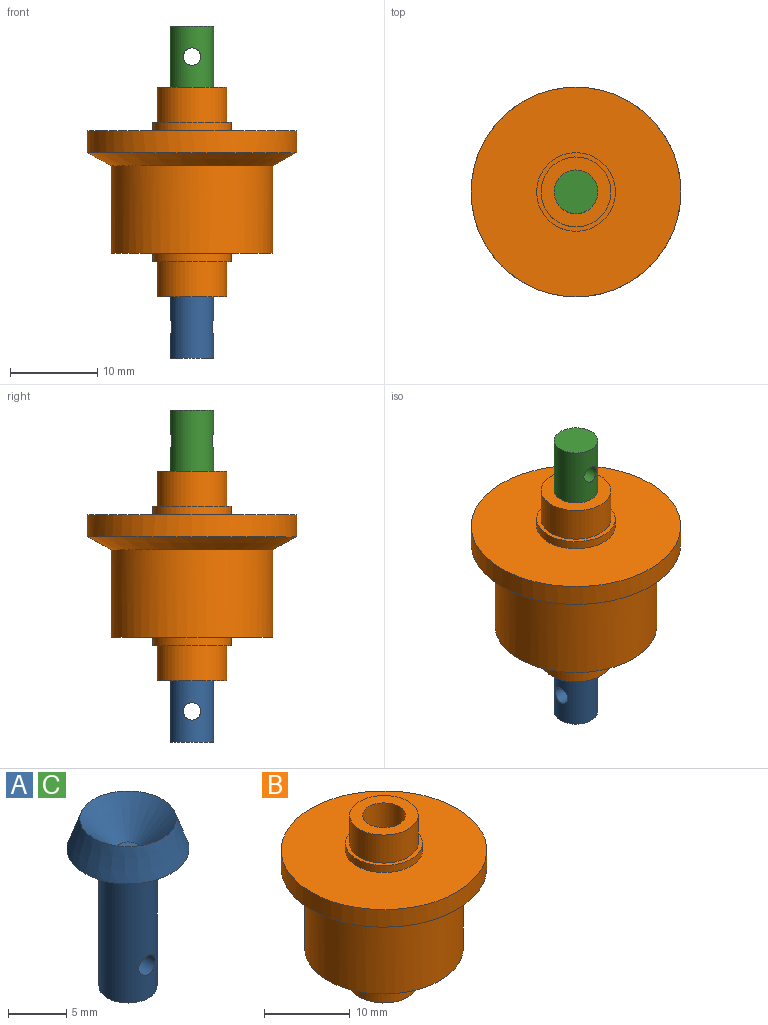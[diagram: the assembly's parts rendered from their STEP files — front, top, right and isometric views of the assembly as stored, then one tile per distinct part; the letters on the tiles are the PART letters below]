
ASSEMBLY  parts=3 mates=2
PART A: 9 faces, bbox 10.5x10.5x17.6 mm
  f0: cylinder r=2.5mm len=14mm, axis (0,0,-1), area 213.5mm2, adj f5,f6,f7
  f1: plane 10.5x10.5mm, normal (0,0,-1), area 58.3mm2, adj f2,f4
  f2: cone r=5.25mm half-angle=19.3deg, axis (0,0,-1), area 98.5mm2, adj f1,f8
  f3: plane 2x2mm, normal (0,0,1), area 3.1mm2, adj f8
  f4: cylinder r=3mm len=6mm, axis (0,0,1), area 9.4mm2, adj f1,f5
  f5: plane 6x6mm, normal (0,0,-1), area 8.6mm2, adj f0,f4
  f6: plane 5x5mm, normal (0,0,-1), area 19.6mm2, adj f0
  f7: cylinder r=1mm len=5mm, axis (0,1,0), area 30.1mm2, adj f0
  f8: cone r=1mm half-angle=45deg, axis (0,0,1), area 72mm2, adj f2,f3
PART B: 15 faces, bbox 24x24x24 mm
  f0: cylinder r=12mm len=24mm, axis (0,0,-1), area 188.5mm2, adj f1,f11
  f1: plane 24x24mm, normal (0,0,1), area 388.8mm2, adj f0,f6
  f2: cylinder r=9.25mm len=18.5mm, axis (0,0,1), area 581.2mm2, adj f3,f12
  f3: plane 18.5x18.5mm, normal (0,0,-1), area 205.2mm2, adj f2,f13
  f4: cylinder r=4mm len=8mm, axis (0,0,1), area 100.5mm2, adj f5,f14
  f5: plane 8x8mm, normal (0,0,-1), area 30.6mm2, adj f4,f10
  f6: cylinder r=4.5mm len=9mm, axis (0,0,-1), area 28.3mm2, adj f1,f7
  f7: plane 9x9mm, normal (0,0,1), area 13.4mm2, adj f6,f9
  f8: plane 8x8mm, normal (0,0,1), area 30.6mm2, adj f9,f10
  f9: cylinder r=4mm len=8mm, axis (0,0,-1), area 100.5mm2, adj f7,f8
  f10: cylinder r=2.5mm len=24mm, axis (0,0,1), area 377mm2, adj f5,f8
  f11: cone r=12mm half-angle=61.4deg, axis (0,0,1), area 209.1mm2, adj f0,f12
  f12: plane 18.5x18.5mm, normal (0,0,1), area 0mm2, adj f2,f11
  f13: cylinder r=4.5mm len=9mm, axis (0,0,1), area 28.3mm2, adj f3,f14
  f14: plane 9x9mm, normal (0,0,-1), area 13.4mm2, adj f4,f13
PART C: same geometry as A
PLACE A rot(axis=(0,0,1),90deg) t=(28.26,17.14,-17.77)mm
PLACE B t=(28.26,17.14,4.23)mm fixed
PLACE C rot(axis=(1,0,0),180deg) t=(28.26,17.14,20.23)mm
MATE revolute A.f0 <-> B.f10  axis (0,0,-1) through (28.26,17.14,-17.77)mm
MATE revolute C.f0 <-> B.f10  axis (0,0,1) through (28.26,17.14,20.23)mm
